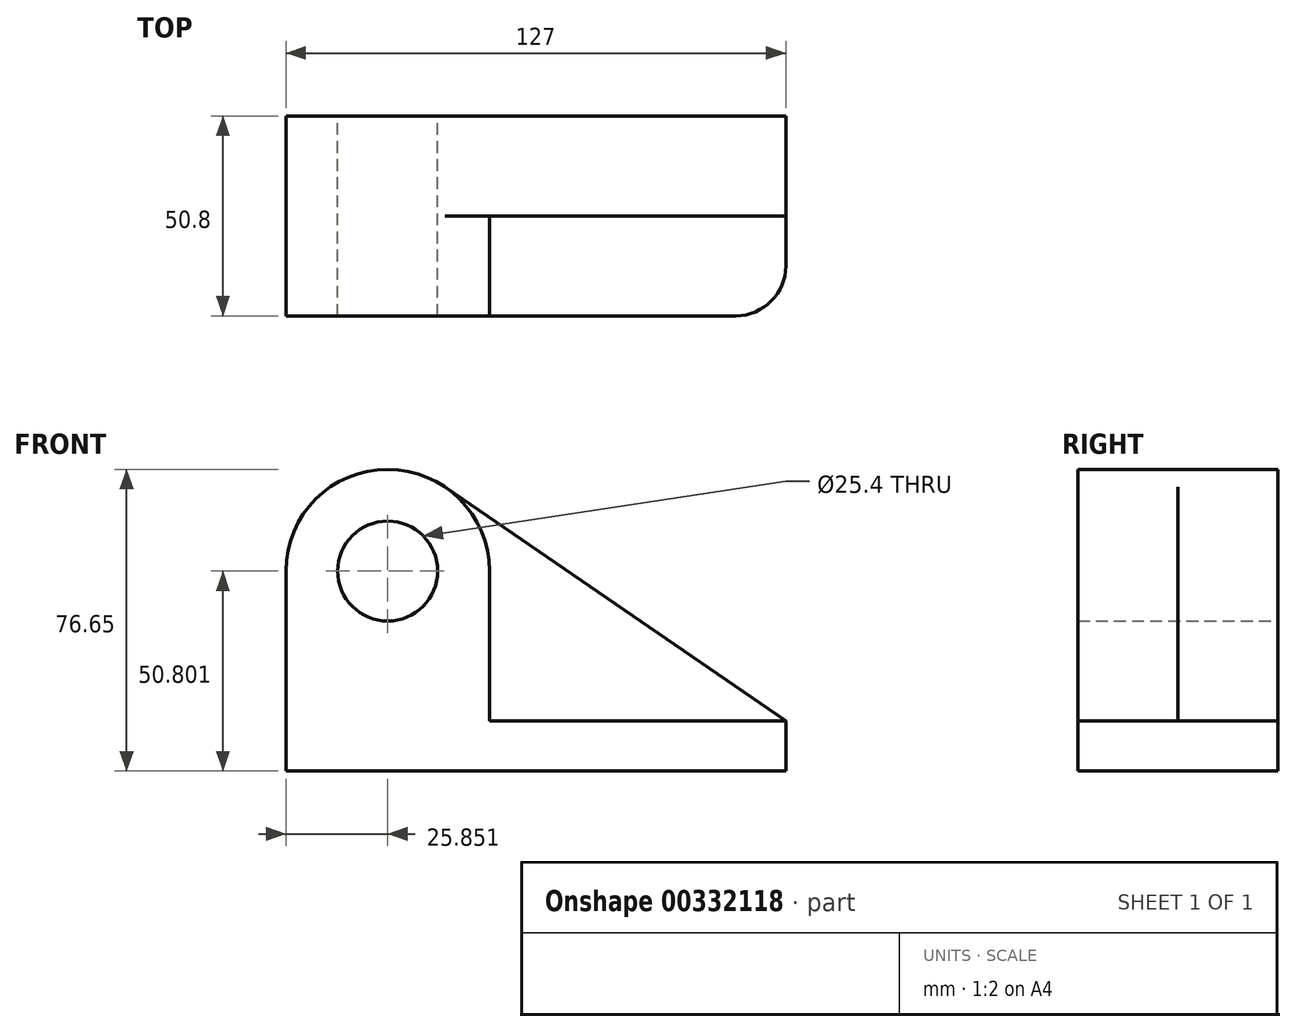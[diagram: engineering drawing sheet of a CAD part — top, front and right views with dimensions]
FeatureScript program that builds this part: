
annotation { "Feature Type Name" : "Feature", "Feature Type Description" : "" }
export const myFeature = defineFeature(function(context is Context, id is Id, definition is map)
    precondition{}
    {
        {
            var Q0;
            Q0=qCreatedBy(makeId("Front.planeOp"),FACE);
            var sketch = newSketch(context, id + "F0", { "sketchPlane" : qUnion([Q0])});
            skCircle(sketch, "E0", {"center": v(-39.93, 22.3) * mm, "radius": 12.7 * mm});
            skArc(sketch, "E1", {"start": v(-25.3, 43.61) * mm, "mid": v(-51.97, 45.18) * mm, "end": v(-65.78, 22.3) * mm});
            skLineSegment(sketch, "E2", {"start": v(-65.78, 22.3) * mm, "end": v(-65.78, -28.5) * mm});
            skLineSegment(sketch, "E3", {"start": v(-65.78, -28.5) * mm, "end": v(61.22, -28.5) * mm});
            skLineSegment(sketch, "E4", {"start": v(61.22, -28.5) * mm, "end": v(61.22, -15.8) * mm});
            skLineSegment(sketch, "E5", {"start": v(61.22, -15.8) * mm, "end": v(-25.3, 43.61) * mm});
            skSolve(sketch);
        }
        {
            var Q0;
            Q0 = qSketchRegion(id + "F0", true);
            extrude(context, id + "F1", {"entities" : qUnion([Q0]), "depth" : 25.4 * mm});
        }
        {
            var Q0;
            Q0=makeQuery(id+"F1.opExtrude","CAP_FACE",FACE,{"disambiguationData":[OSD([sQuery(id+"F0.wireOp",EDGE,"E0"),sQuery(id+"F0.wireOp",EDGE,"E1"),sQuery(id+"F0.wireOp",EDGE,"E2"),sQuery(id+"F0.wireOp",EDGE,"E3"),sQuery(id+"F0.wireOp",EDGE,"E4"),sQuery(id+"F0.wireOp",EDGE,"E5")])],"isStart":false});
            var sketch = newSketch(context, id + "F2", { "sketchPlane" : qUnion([Q0])});
            skCircle(sketch, "E6", {"center": v(-39.93, 22.3) * mm, "radius": 12.7 * mm});
            skLineSegment(sketch, "E7.bottom", {"start": v(61.22, -15.8) * mm, "end": v(-14.08, -15.8) * mm});
            skLineSegment(sketch, "E7.top", {"start": v(61.22, -28.5) * mm, "end": v(-65.78, -28.5) * mm});
            skLineSegment(sketch, "E7.left", {"start": v(61.22, -15.8) * mm, "end": v(61.22, -28.5) * mm});
            skLineSegment(sketch, "E7.right", {"start": v(-65.78, -15.8) * mm, "end": v(-65.78, -28.5) * mm});
            skArc(sketch, "E8", {"start": v(-14.08, 22.3) * mm, "mid": v(-39.93, 48.15) * mm, "end": v(-65.78, 22.3) * mm});
            skLineSegment(sketch, "E9", {"start": v(-65.78, 22.3) * mm, "end": v(-65.78, -15.8) * mm});
            skLineSegment(sketch, "E10", {"start": v(-14.08, 22.3) * mm, "end": v(-14.08, -15.8) * mm});
            skSolve(sketch);
        }
        {
            var Q0;
            Q0=makeQuery(id+"F2.imprint","IMPRINT",FACE,{"disambiguationData":[TD([[makeQuery(id+"F2.imprint","IMPRINT",EDGE,{"derivedFrom":sQuery(id+"F2.wireOp",EDGE,"E6")}),-1.0]])]});
            extrude(context, id + "F3", {"entities" : qUnion([Q0]), "operationType" : NewBodyOperationType.ADD, "depth" : 25.4 * mm});
        }
        {
            var Q0;
            Q0=makeQuery(id+"F3.opExtrude","CAP_EDGE",EDGE,{"disambiguationData":[OSD([sQuery(id+"F2.wireOp",EDGE,"E7.left")])],"isStart":false});
            fillet(context, id + "F4", {"entities" : qUnion([Q0]), "radius" : 12.7 * mm, "tangentPropagation" : true, "allowEdgeOverflow" : false});
        }
    });
